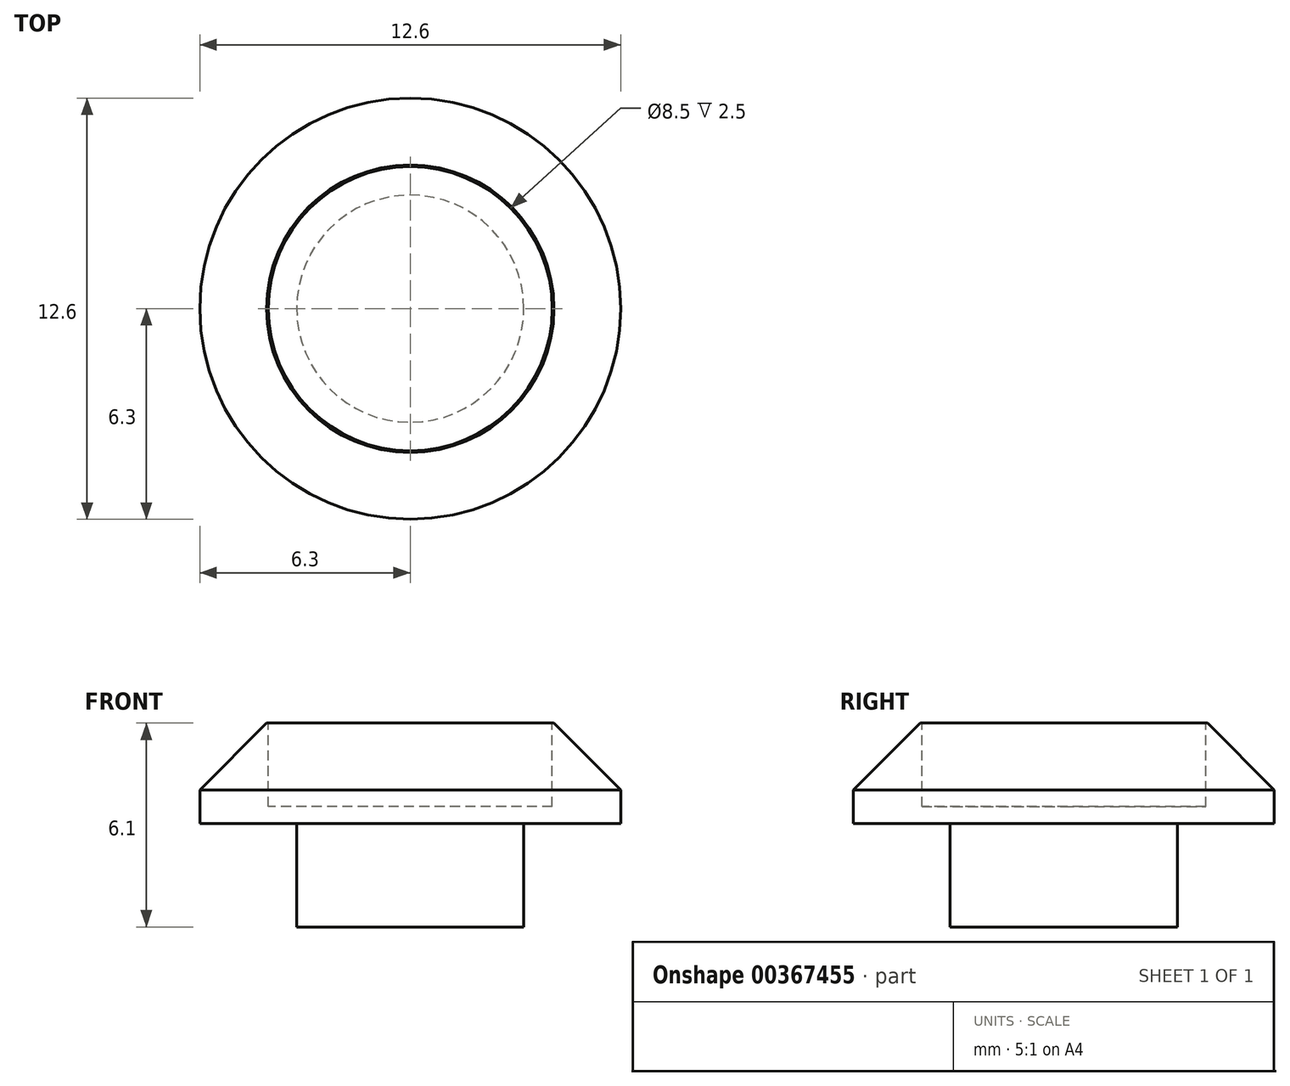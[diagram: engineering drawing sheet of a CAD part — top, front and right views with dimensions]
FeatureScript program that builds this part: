
annotation { "Feature Type Name" : "Feature", "Feature Type Description" : "" }
export const myFeature = defineFeature(function(context is Context, id is Id, definition is map)
    precondition{}
    {
        {
            var Q0;
            Q0=qCreatedBy(makeId("Top.planeOp"),FACE);
            var sketch = newSketch(context, id + "F0", { "sketchPlane" : qUnion([Q0])});
            skCircle(sketch, "E0", {"center": v(0, 0) * mm, "radius": 3.4 * mm});
            skSolve(sketch);
        }
        {
            var Q0;
            Q0=qSketchRegion(id+"F0",true);
            extrude(context, id + "F1", {"entities" : qUnion([Q0]), "depth" : 3.1 * mm});
        }
        {
            var Q0;
            Q0=makeQuery(id+"F1.opExtrude","CAP_FACE",FACE,{"disambiguationData":[OSD([sQuery(id+"F0.wireOp",EDGE,"E0")])],"isStart":false});
            var sketch = newSketch(context, id + "F2", { "sketchPlane" : qUnion([Q0])});
            skCircle(sketch, "E1", {"center": v(0, 0) * mm, "radius": 6.3 * mm});
            skSolve(sketch);
        }
        {
            var Q0;
            Q0=qSketchRegion(id+"F2",true);
            extrude(context, id + "F3", {"entities" : qUnion([Q0]), "operationType" : NewBodyOperationType.ADD, "depth" : 3 * mm});
        }
        {
            var Q0;
            Q0=makeQuery(id+"F3.opExtrude","CAP_EDGE",EDGE,{"disambiguationData":[OSD([sQuery(id+"F2.wireOp",EDGE,"E1")])],"isStart":false});
            chamfer(context, id + "F4", {"entities" : qUnion([Q0]), "width" : 2 * mm, "tangentPropagation" : true});
        }
        {
            var Q0;
            Q0=makeQuery(id+"F3.opExtrude","CAP_FACE",FACE,{"disambiguationData":[OSD([sQuery(id+"F2.wireOp",EDGE,"E1")])],"isStart":false});
            var sketch = newSketch(context, id + "F5", { "sketchPlane" : qUnion([Q0])});
            skCircle(sketch, "E2", {"center": v(0, 0) * mm, "radius": 4.25 * mm});
            skSolve(sketch);
        }
        {
            var Q0;
            Q0=qSketchRegion(id+"F5",true);
            extrude(context, id + "F6", {"entities" : qUnion([Q0]), "operationType" : NewBodyOperationType.REMOVE, "oppositeDirection" : true, "depth" : 2.5 * mm});
        }
    });
